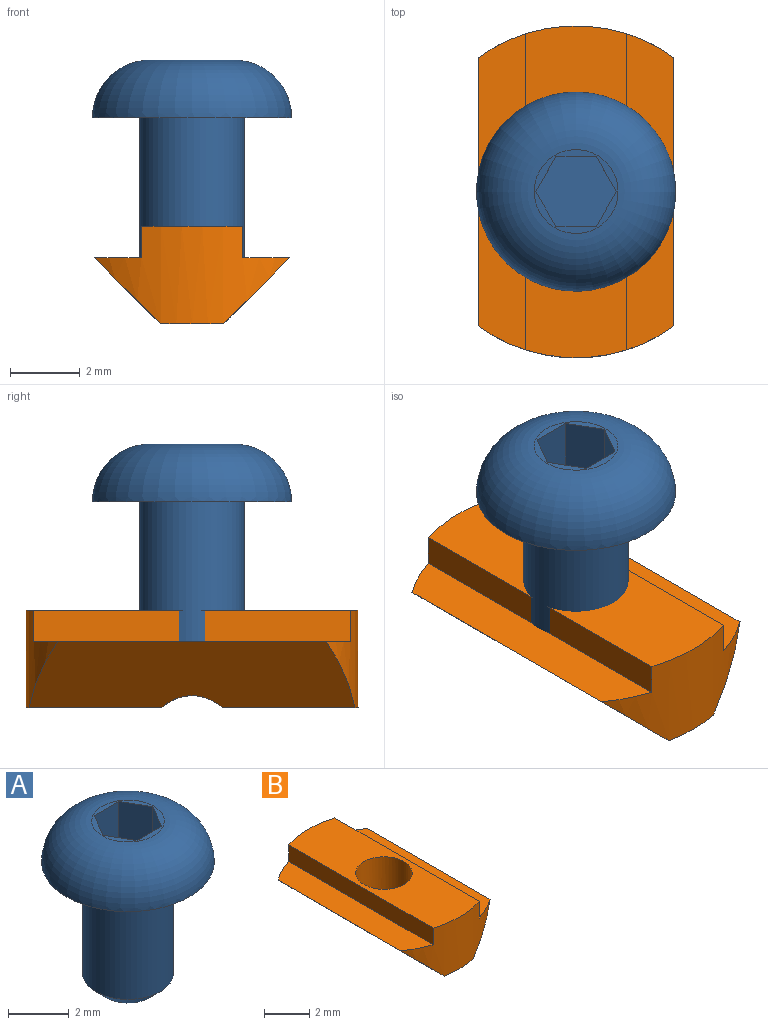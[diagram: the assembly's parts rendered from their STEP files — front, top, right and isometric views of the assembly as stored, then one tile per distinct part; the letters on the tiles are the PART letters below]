
ASSEMBLY  parts=2 mates=1
PART A: 13 faces, bbox 5.7x5.7x6.7 mm
  f0: plane 2.4x2.4mm, normal (0,0,1), area 1.1mm2, adj f2,f3,f4,f5,f6,f7,f8
  f1: plane 5.7x5.7mm, normal (0,0,-1), area 18.4mm2, adj f2,f10
  f2: torus R=1.2mm, axis (0,0,-1), area 36.6mm2, adj f0,f1
  f3: plane 1.5x1mm, normal (-0.87,-0.5,0), area 1.7mm2, adj f0,f4,f8,f9
  f4: plane 1.5x1.15mm, normal (0,-1,0), area 1.7mm2, adj f0,f3,f5,f9
  f5: plane 1.5x1mm, normal (0.87,-0.5,0), area 1.7mm2, adj f0,f4,f6,f9
  f6: plane 1.5x1mm, normal (0.87,0.5,0), area 1.7mm2, adj f0,f5,f7,f9
  f7: plane 1.5x1.15mm, normal (0,1,0), area 1.7mm2, adj f0,f6,f8,f9
  f8: plane 1.5x1mm, normal (-0.87,0.5,0), area 1.7mm2, adj f0,f3,f7,f9
  f9: plane 2.31x2mm, normal (0,0,1), area 3.5mm2, adj f3,f4,f5,f6,f7,f8
  f10: cylinder r=1.5mm len=4.5mm, axis (0,0,1), area 42.4mm2, adj f1,f12
  f11: plane 2x2mm, normal (0,0,-1), area 3.1mm2, adj f12
  f12: cone r=1mm half-angle=45deg, axis (0,0,1), area 5.6mm2, adj f10,f11
PART B: 12 faces, bbox 5.6x9.5x2.8 mm
  f0: plane 3.88x1.8mm, normal (0,0,-1), area 6.5mm2, adj f4,f6,f9,f11
  f1: plane 9.5x2.9mm, normal (0,0,1), area 22.2mm2, adj f2,f8,f9,f10,f11
  f2: plane 9.05x0.9mm, normal (-1,0,0), area 8.1mm2, adj f1,f3,f9,f10
  f3: plane 9.05x1.35mm, normal (0,0,1), area 11.4mm2, adj f2,f4,f9,f10
  f4: plane 9.33x1.9mm, normal (-0.71,0,-0.71), area 22.7mm2, adj f0,f3,f5,f9,f10,f11
  f5: plane 3.88x1.8mm, normal (0,0,-1), area 6.5mm2, adj f4,f6,f10,f11
  f6: plane 9.33x1.9mm, normal (0.71,0,-0.71), area 22.7mm2, adj f0,f5,f7,f9,f10,f11
  f7: plane 9.05x1.35mm, normal (0,0,1), area 11.4mm2, adj f6,f8,f9,f10
  f8: plane 9.05x0.9mm, normal (1,0,0), area 8.1mm2, adj f1,f7,f9,f10
  f9: cylinder r=4.75mm len=5.6mm, axis (0,0,1), area 9.9mm2, adj f0,f1,f2,f3,f4,f6,f7,f8
  f10: cylinder r=4.75mm len=5.6mm, axis (0,0,1), area 9.9mm2, adj f1,f2,f3,f4,f5,f6,f7,f8
  f11: cylinder r=1.25mm len=2.8mm, axis (0,0,1), area 21.1mm2, adj f0,f1,f4,f5,f6
PLACE A t=(0,0,3.1)mm
PLACE B at identity fixed
MATE fastened B.f9 <-> A.f2  axis (0,0,1) through (0,0,0)mm
